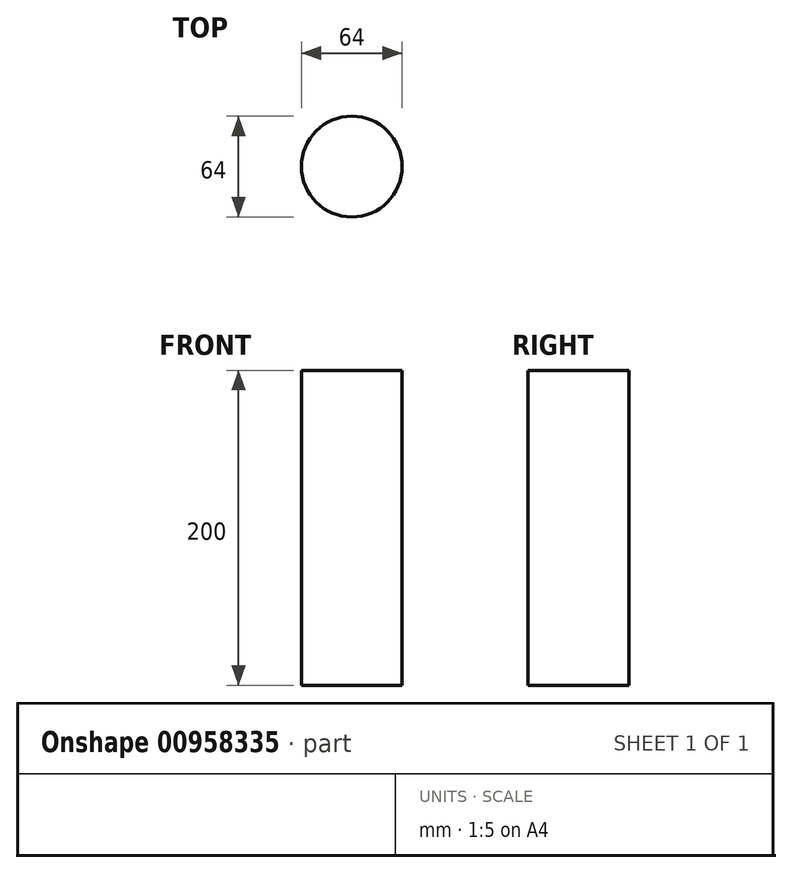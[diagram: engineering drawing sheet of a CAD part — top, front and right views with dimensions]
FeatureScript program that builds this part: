
annotation { "Feature Type Name" : "Feature", "Feature Type Description" : "" }
export const myFeature = defineFeature(function(context is Context, id is Id, definition is map)
    precondition{}
    {
        {
            var Q0;
            Q0=qCreatedBy(makeId("Top.planeOp"),FACE);
            var sketch = newSketch(context, id + "F0", { "sketchPlane" : qUnion([Q0])});
            skCircle(sketch, "E0", {"center": v(0, 0) * mm, "radius": 32 * mm});
            skSolve(sketch);
        }
        {
            var Q0;
            Q0=makeQuery(id+"F0.imprint","IMPRINT",FACE,{"disambiguationData":[TD([[makeQuery(id+"F0.imprint","IMPRINT",EDGE,{"derivedFrom":sQuery(id+"F0.wireOp",EDGE,"E0")}),1.0]])]});
            extrude(context, id + "F1", {"entities" : qUnion([Q0]), "depth" : 200 * mm, "offsetDistance" : 25 * mm});
        }
        {
            var Q0;
            Q0=makeQuery(id+"F1.opExtrude","CAP_FACE",FACE,{"disambiguationData":[OSD([sQuery(id+"F0.wireOp",EDGE,"E0")])],"isStart":false});
            cPlane(context, id + "F2", {"entities" : qUnion([Q0]), "cplaneType" : CPlaneType.OFFSET, "offset" : 0 * mm, "width" : 150 * mm, "height" : 150 * mm});
        }
    });
